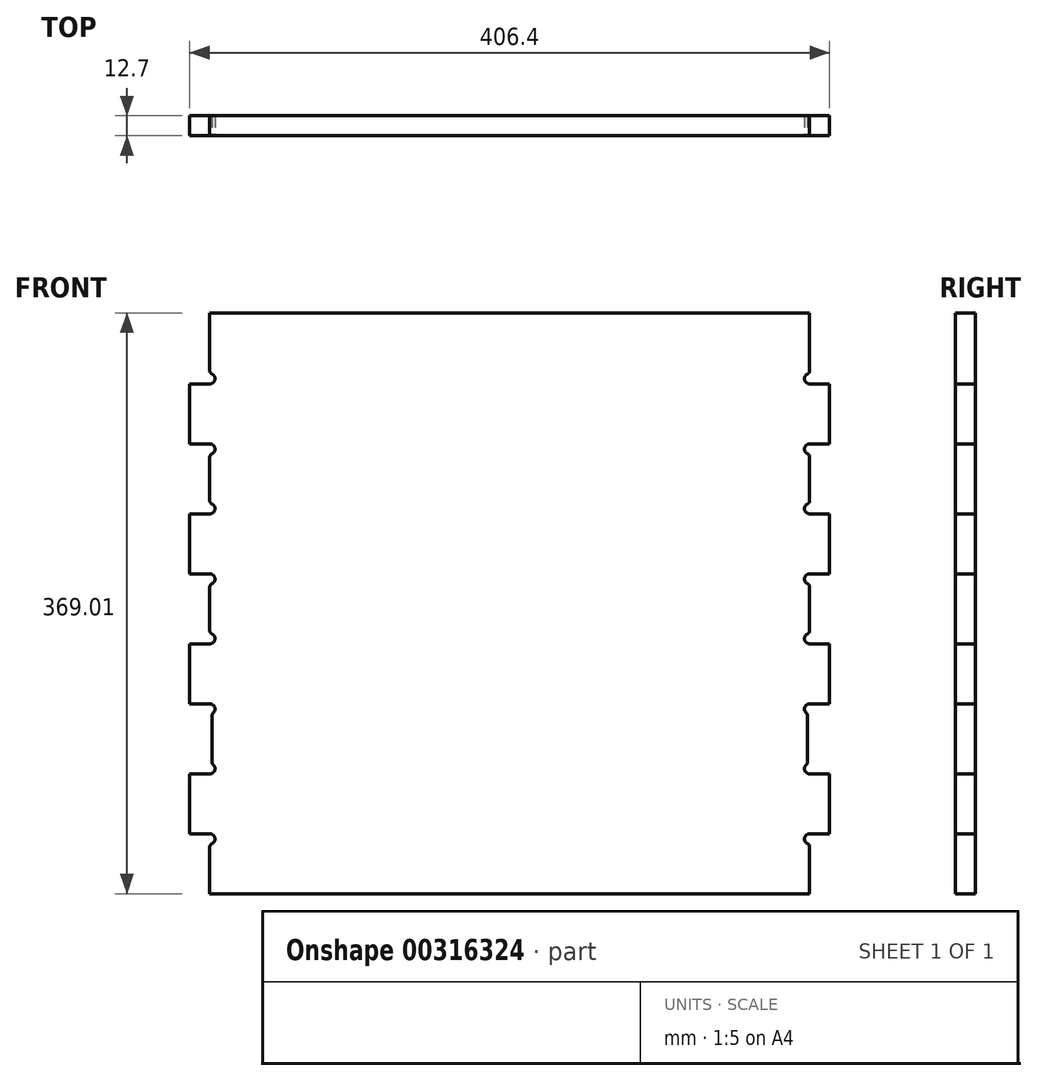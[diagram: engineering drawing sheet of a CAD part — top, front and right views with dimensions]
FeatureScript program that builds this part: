
annotation { "Feature Type Name" : "Feature", "Feature Type Description" : "" }
export const myFeature = defineFeature(function(context is Context, id is Id, definition is map)
    precondition{}
    {
        {
            var Q0;
            Q0=qCreatedBy(makeId("Front.planeOp"),FACE);
            var sketch = newSketch(context, id + "F0", { "sketchPlane" : qUnion([Q0])});
            skLineSegment(sketch, "E0.bottom", {"start": v(0, 0) * mm, "end": v(406.4, 0) * mm});
            skLineSegment(sketch, "E0.top", {"start": v(0, 369.01) * mm, "end": v(406.4, 369.01) * mm});
            skLineSegment(sketch, "E0.left", {"start": v(0, 0) * mm, "end": v(0, 369.01) * mm});
            skLineSegment(sketch, "E0.right", {"start": v(406.4, 0) * mm, "end": v(406.4, 369.01) * mm});
            skSolve(sketch);
        }
        {
            var Q0;
            Q0 = qSketchRegion(id + "F0", true);
            extrude(context, id + "F1", {"entities" : qUnion([Q0]), "depth" : 12.7 * mm});
        }
        {
            var Q0;
            Q0=makeQuery(id+"F1.opExtrude","CAP_FACE",FACE,{"disambiguationData":[OSD([sQuery(id+"F0.wireOp",EDGE,"E0.bottom"),sQuery(id+"F0.wireOp",EDGE,"E0.top"),sQuery(id+"F0.wireOp",EDGE,"E0.left"),sQuery(id+"F0.wireOp",EDGE,"E0.right")])],"isStart":false});
            var sketch = newSketch(context, id + "F2", { "sketchPlane" : qUnion([Q0])});
            skLineSegment(sketch, "E1", {"start": v(203.2, 369.01) * mm, "end": v(203.2, 0) * mm, "construction": true});
            skLineSegment(sketch, "E2.bottom", {"start": v(0, 0) * mm, "end": v(12.7, 0) * mm});
            skLineSegment(sketch, "E2.top", {"start": v(0, 38.1) * mm, "end": v(12.7, 38.1) * mm});
            skLineSegment(sketch, "E2.left", {"start": v(0, 0) * mm, "end": v(0, 38.1) * mm});
            skLineSegment(sketch, "E2.right", {"start": v(12.7, 0) * mm, "end": v(12.7, 29.87) * mm});
            skLineSegment(sketch, "E3.bottom", {"start": v(0, 76.2) * mm, "end": v(12.7, 76.2) * mm});
            skLineSegment(sketch, "E3.top", {"start": v(0, 120.65) * mm, "end": v(12.7, 120.65) * mm});
            skLineSegment(sketch, "E3.left", {"start": v(0, 76.2) * mm, "end": v(0, 120.65) * mm});
            skLineSegment(sketch, "E4.direction1", {"start": v(0, 76.2) * mm, "end": v(25.4, 76.2) * mm, "construction": true});
            skLineSegment(sketch, "E4.direction2", {"start": v(0, 76.2) * mm, "end": v(0, 158.75) * mm, "construction": true});
            skLineSegment(sketch, "E5.bottom", {"start": v(0, 203.2) * mm, "end": v(12.7, 203.2) * mm});
            skLineSegment(sketch, "E5.top", {"start": v(0, 158.75) * mm, "end": v(12.7, 158.75) * mm});
            skLineSegment(sketch, "E5.left", {"start": v(0, 203.2) * mm, "end": v(0, 158.75) * mm});
            skLineSegment(sketch, "E5.right", {"start": v(12.7, 194.97) * mm, "end": v(12.7, 166.98) * mm});
            skLineSegment(sketch, "E6.bottom", {"start": v(0, 285.75) * mm, "end": v(12.7, 285.75) * mm});
            skLineSegment(sketch, "E6.top", {"start": v(0, 241.3) * mm, "end": v(12.7, 241.3) * mm});
            skLineSegment(sketch, "E6.left", {"start": v(0, 285.75) * mm, "end": v(0, 241.3) * mm});
            skLineSegment(sketch, "E7.bottom", {"start": v(0, 323.85) * mm, "end": v(12.7, 323.85) * mm});
            skLineSegment(sketch, "E7.top", {"start": v(0, 369.01) * mm, "end": v(12.7, 369.01) * mm});
            skLineSegment(sketch, "E7.left", {"start": v(0, 323.85) * mm, "end": v(0, 369.01) * mm});
            skArc(sketch, "E8", {"start": v(12.7, 323.85) * mm, "mid": v(15.94, 326.51) * mm, "end": v(13.96, 330.2) * mm});
            skArc(sketch, "E9", {"start": v(13.96, 279.4) * mm, "mid": v(15.94, 283.09) * mm, "end": v(12.7, 285.75) * mm});
            skLineSegment(sketch, "E10.trimOffspring", {"start": v(12.7, 332.08) * mm, "end": v(12.7, 369.01) * mm});
            skLineSegment(sketch, "E11.trimOffspring", {"start": v(12.7, 277.52) * mm, "end": v(12.7, 249.53) * mm});
            skArc(sketch, "E12", {"start": v(12.7, 241.3) * mm, "mid": v(15.94, 243.96) * mm, "end": v(13.96, 247.66) * mm});
            skArc(sketch, "E13", {"start": v(13.96, 196.84) * mm, "mid": v(15.94, 200.54) * mm, "end": v(12.7, 203.2) * mm});
            skArc(sketch, "E14", {"start": v(12.7, 158.75) * mm, "mid": v(15.94, 161.41) * mm, "end": v(13.96, 165.1) * mm});
            skArc(sketch, "E15", {"start": v(12.7, 76.2) * mm, "mid": v(15.8, 78.34) * mm, "end": v(14.87, 81.99) * mm});
            skArc(sketch, "E16", {"start": v(13.96, 31.74) * mm, "mid": v(15.94, 35.44) * mm, "end": v(12.7, 38.1) * mm});
            skArc(sketch, "E17", {"start": v(14.87, 114.86) * mm, "mid": v(15.8, 118.5) * mm, "end": v(12.7, 120.65) * mm});
            skLineSegment(sketch, "E18", {"start": v(14.18, 113.33) * mm, "end": v(14.18, 83.52) * mm});
            skPoint(sketch, "E19.visualSharp", {"position": v(14.18, 114.4) * mm});
            skArc(sketch, "E19.filletArc", {"start": v(14.87, 114.86) * mm, "mid": v(14.36, 114.17) * mm, "end": v(14.18, 113.33) * mm});
            skPoint(sketch, "E20.visualSharp", {"position": v(14.18, 82.46) * mm});
            skArc(sketch, "E20.filletArc", {"start": v(14.18, 83.52) * mm, "mid": v(14.36, 82.68) * mm, "end": v(14.87, 81.99) * mm});
            skPoint(sketch, "E21.visualSharp", {"position": v(12.7, 31.5) * mm});
            skArc(sketch, "E21.filletArc", {"start": v(13.96, 31.74) * mm, "mid": v(13.04, 31) * mm, "end": v(12.7, 29.87) * mm});
            skPoint(sketch, "E22.visualSharp", {"position": v(12.7, 165.35) * mm});
            skArc(sketch, "E22.filletArc", {"start": v(12.7, 166.98) * mm, "mid": v(13.04, 165.85) * mm, "end": v(13.96, 165.1) * mm});
            skPoint(sketch, "E23.visualSharp", {"position": v(12.7, 196.6) * mm});
            skArc(sketch, "E23.filletArc", {"start": v(13.96, 196.84) * mm, "mid": v(13.04, 196.1) * mm, "end": v(12.7, 194.97) * mm});
            skPoint(sketch, "E24.visualSharp", {"position": v(12.7, 247.9) * mm});
            skArc(sketch, "E24.filletArc", {"start": v(12.7, 249.53) * mm, "mid": v(13.04, 248.4) * mm, "end": v(13.96, 247.66) * mm});
            skPoint(sketch, "E25.visualSharp", {"position": v(12.7, 279.15) * mm});
            skArc(sketch, "E25.filletArc", {"start": v(13.96, 279.4) * mm, "mid": v(13.04, 278.65) * mm, "end": v(12.7, 277.52) * mm});
            skPoint(sketch, "E26.visualSharp", {"position": v(12.7, 330.45) * mm});
            skArc(sketch, "E26.filletArc", {"start": v(12.7, 332.08) * mm, "mid": v(13.04, 330.95) * mm, "end": v(13.96, 330.2) * mm});
            skArc(sketch, "E27.MirrorCS", {"start": v(393.7, 249.53) * mm, "mid": v(393.36, 248.4) * mm, "end": v(392.44, 247.66) * mm});
            skArc(sketch, "E28.MirrorCS", {"start": v(393.7, 166.98) * mm, "mid": v(393.36, 165.85) * mm, "end": v(392.44, 165.1) * mm});
            skArc(sketch, "E29.MirrorCS", {"start": v(392.44, 31.74) * mm, "mid": v(393.36, 31) * mm, "end": v(393.7, 29.87) * mm});
            skArc(sketch, "E30.MirrorCS", {"start": v(393.7, 241.3) * mm, "mid": v(390.46, 243.96) * mm, "end": v(392.44, 247.66) * mm});
            skArc(sketch, "E31.MirrorCS", {"start": v(393.7, 76.2) * mm, "mid": v(390.6, 78.34) * mm, "end": v(391.53, 81.99) * mm});
            skArc(sketch, "E32.MirrorCS", {"start": v(391.53, 114.86) * mm, "mid": v(392.04, 114.17) * mm, "end": v(392.22, 113.33) * mm});
            skArc(sketch, "E33.MirrorCS", {"start": v(392.44, 196.84) * mm, "mid": v(393.36, 196.1) * mm, "end": v(393.7, 194.97) * mm});
            skArc(sketch, "E34.MirrorCS", {"start": v(392.22, 83.52) * mm, "mid": v(392.04, 82.68) * mm, "end": v(391.53, 81.99) * mm});
            skArc(sketch, "E35.MirrorCS", {"start": v(392.44, 279.4) * mm, "mid": v(393.36, 278.65) * mm, "end": v(393.7, 277.52) * mm});
            skArc(sketch, "E36.MirrorCS", {"start": v(393.7, 323.85) * mm, "mid": v(390.46, 326.51) * mm, "end": v(392.44, 330.2) * mm});
            skArc(sketch, "E37.MirrorCS", {"start": v(393.7, 332.08) * mm, "mid": v(393.36, 330.95) * mm, "end": v(392.44, 330.2) * mm});
            skArc(sketch, "E38.MirrorCS", {"start": v(392.44, 196.84) * mm, "mid": v(390.46, 200.54) * mm, "end": v(393.7, 203.2) * mm});
            skArc(sketch, "E39.MirrorCS", {"start": v(392.44, 31.74) * mm, "mid": v(390.46, 35.44) * mm, "end": v(393.7, 38.1) * mm});
            skArc(sketch, "E40.MirrorCS", {"start": v(392.44, 279.4) * mm, "mid": v(390.46, 283.09) * mm, "end": v(393.7, 285.75) * mm});
            skArc(sketch, "E41.MirrorCS", {"start": v(391.53, 114.86) * mm, "mid": v(390.6, 118.5) * mm, "end": v(393.7, 120.65) * mm});
            skArc(sketch, "E42.MirrorCS", {"start": v(393.7, 158.75) * mm, "mid": v(390.46, 161.41) * mm, "end": v(392.44, 165.1) * mm});
            skLineSegment(sketch, "E43.MirrorCS", {"start": v(406.4, 158.75) * mm, "end": v(393.7, 158.75) * mm});
            skLineSegment(sketch, "E44.MirrorCS", {"start": v(406.4, 38.1) * mm, "end": v(393.7, 38.1) * mm});
            skLineSegment(sketch, "E45.MirrorCS", {"start": v(406.4, 203.2) * mm, "end": v(393.7, 203.2) * mm});
            skLineSegment(sketch, "E46.MirrorCS", {"start": v(406.4, 76.2) * mm, "end": v(393.7, 76.2) * mm});
            skLineSegment(sketch, "E47.MirrorCS", {"start": v(406.4, 323.85) * mm, "end": v(393.7, 323.85) * mm});
            skPoint(sketch, "E48.MirrorP", {"position": v(393.7, 196.6) * mm});
            skLineSegment(sketch, "E49.MirrorCS", {"start": v(406.4, 241.3) * mm, "end": v(393.7, 241.3) * mm});
            skLineSegment(sketch, "E50.MirrorCS", {"start": v(406.4, 76.2) * mm, "end": v(406.4, 120.65) * mm});
            skPoint(sketch, "E51.MirrorP", {"position": v(393.7, 165.35) * mm});
            skPoint(sketch, "E52.MirrorP", {"position": v(392.22, 82.46) * mm});
            skPoint(sketch, "E53.MirrorP", {"position": v(393.7, 330.45) * mm});
            skPoint(sketch, "E54.MirrorP", {"position": v(393.7, 31.5) * mm});
            skPoint(sketch, "E55.MirrorP", {"position": v(392.22, 114.4) * mm});
            skLineSegment(sketch, "E56.MirrorCS", {"start": v(406.4, 285.75) * mm, "end": v(393.7, 285.75) * mm});
            skLineSegment(sketch, "E57.MirrorCS", {"start": v(406.4, 120.65) * mm, "end": v(393.7, 120.65) * mm});
            skPoint(sketch, "E58.MirrorP", {"position": v(393.7, 247.9) * mm});
            skLineSegment(sketch, "E59.MirrorCS", {"start": v(406.4, 76.2) * mm, "end": v(406.4, 158.75) * mm, "construction": true});
            skLineSegment(sketch, "E60.MirrorCS", {"start": v(406.4, 76.2) * mm, "end": v(381, 76.2) * mm, "construction": true});
            skPoint(sketch, "E61.MirrorP", {"position": v(393.7, 279.15) * mm});
            skLineSegment(sketch, "E62.MirrorCS", {"start": v(406.4, 369.01) * mm, "end": v(393.7, 369.01) * mm});
            skLineSegment(sketch, "E63.MirrorCS", {"start": v(393.7, 194.97) * mm, "end": v(393.7, 166.98) * mm});
            skLineSegment(sketch, "E64.MirrorCS", {"start": v(406.4, 285.75) * mm, "end": v(406.4, 241.3) * mm});
            skLineSegment(sketch, "E65.MirrorCS", {"start": v(393.7, 277.52) * mm, "end": v(393.7, 249.53) * mm});
            skLineSegment(sketch, "E66.MirrorCS", {"start": v(393.7, 332.08) * mm, "end": v(393.7, 369.01) * mm});
            skLineSegment(sketch, "E67.MirrorCS", {"start": v(406.4, 203.2) * mm, "end": v(406.4, 158.75) * mm});
            skLineSegment(sketch, "E68.MirrorCS", {"start": v(393.7, 0) * mm, "end": v(393.7, 29.87) * mm});
            skLineSegment(sketch, "E69.MirrorCS", {"start": v(406.4, 323.85) * mm, "end": v(406.4, 369.01) * mm});
            skLineSegment(sketch, "E70.MirrorCS", {"start": v(392.22, 113.33) * mm, "end": v(392.22, 83.52) * mm});
            skLineSegment(sketch, "E71.MirrorCS", {"start": v(406.4, 0) * mm, "end": v(393.7, 0) * mm});
            skLineSegment(sketch, "E72.MirrorCS", {"start": v(406.4, 0) * mm, "end": v(406.4, 38.1) * mm});
            skSolve(sketch);
        }
        {
            var Q0;
            Q0 = qSketchRegion(id + "F2", true);
            extrude(context, id + "F3", {"entities" : qUnion([Q0]), "operationType" : NewBodyOperationType.REMOVE, "oppositeDirection" : true, "depth" : 25.4 * mm});
        }
    });
